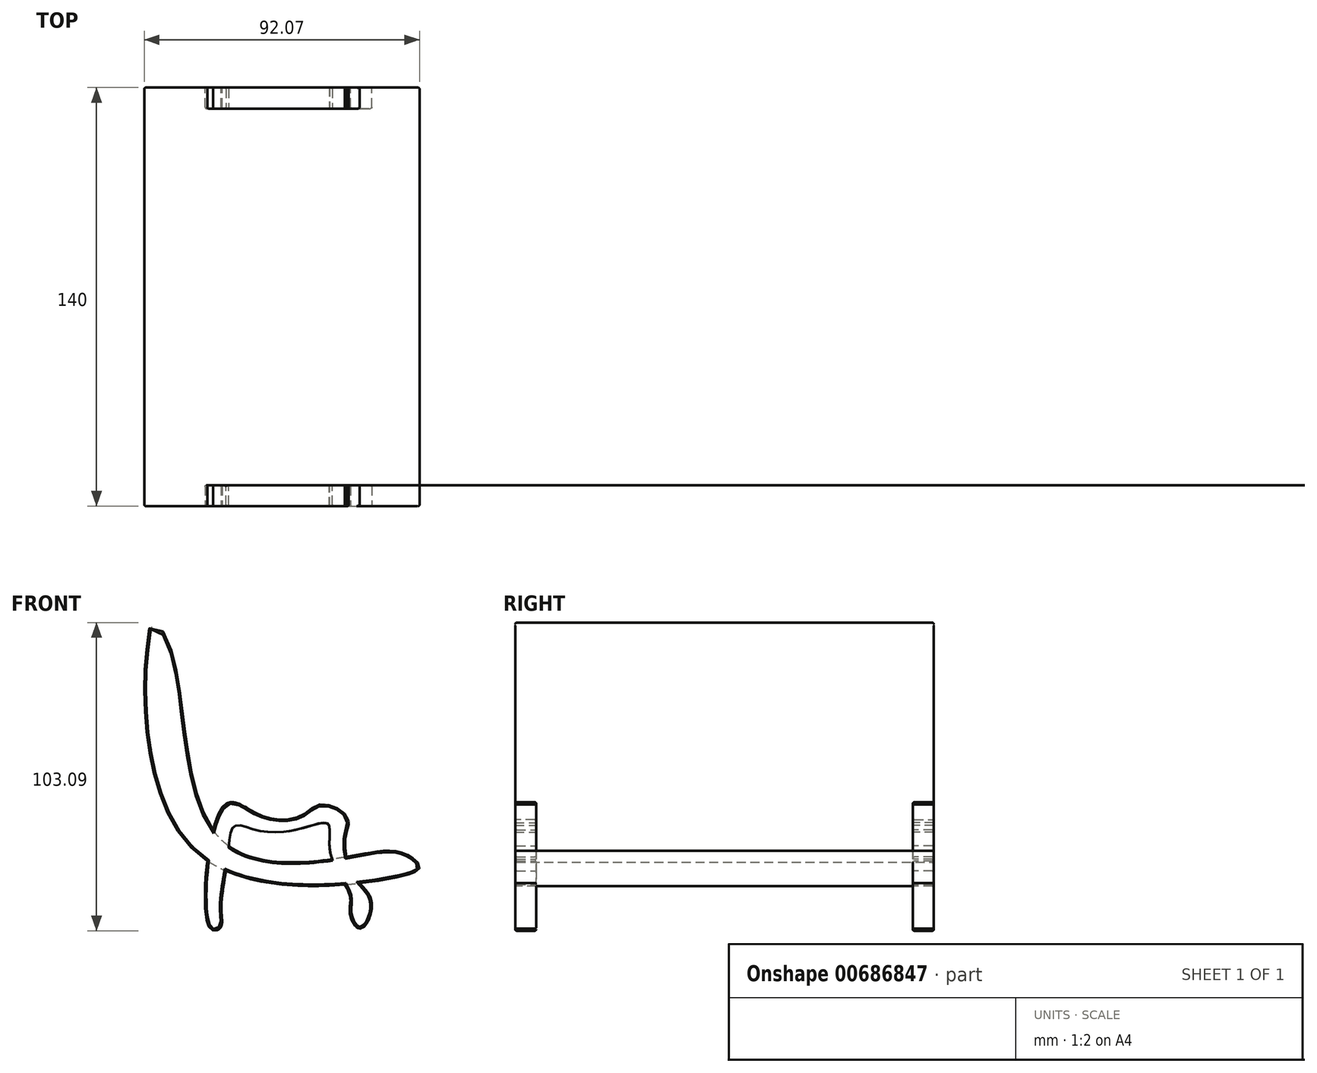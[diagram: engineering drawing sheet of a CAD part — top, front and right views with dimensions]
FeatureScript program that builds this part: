
annotation { "Feature Type Name" : "Feature", "Feature Type Description" : "" }
export const myFeature = defineFeature(function(context is Context, id is Id, definition is map)
    precondition{}
    {
        {
            var Q0;
            Q0=qCreatedBy(makeId("Front.planeOp"),FACE);
            var sketch = newSketch(context, id + "F0", { "sketchPlane" : qUnion([Q0])});
            skFitSpline(sketch, "E0", {"points": [v(-47.91, 42.75) * mm, v(-30.7, -20.37) * mm, v(37, -28.4) * mm, v(43.9, -24.96) * mm, v(38.16, -20.37) * mm, v(20.94, -21.52) * mm, v(-22.66, -15.78) * mm, v(-38.73, 46.2) * mm, v(-45.62, 56.52) * mm, v(-46.76, 51.93) * mm, v(-47.91, 42.75) * mm]});
            skSolve(sketch);
        }
        {
            var Q0;
            Q0 = qSketchRegion(id + "F0", true);
            extrude(context, id + "F1", {"entities" : qUnion([Q0]), "depth" : 70 * mm, "offsetDistance" : 25.4 * mm});
        }
        {
            var Q0;
            Q0=qCreatedBy(makeId("Front.planeOp"),FACE);
            cPlane(context, id + "F2", {"entities" : qUnion([Q0]), "cplaneType" : CPlaneType.OFFSET, "offset" : 63 * mm, "width" : 150 * mm, "height" : 150 * mm});
        }
        {
            var Q0;
            Q0=qCreatedBy(id+"F2.planeOp",FACE);
            var sketch = newSketch(context, id + "F3", { "sketchPlane" : qUnion([Q0])});
            skFitSpline(sketch, "E1", {"points": [v(-27.53, -41.38) * mm, v(-20.96, -4.2) * mm, v(-9.3, -7.84) * mm, v(4.56, -7.84) * mm, v(11.12, -4.2) * mm, v(19.87, -8.57) * mm, v(19.14, -15.13) * mm, v(22.06, -28.26) * mm, v(27.9, -37) * mm, v(24.24, -45.76) * mm, v(20.6, -40.65) * mm, v(20.6, -34.82) * mm, v(14.04, -20.23) * mm, v(13.3, -10.76) * mm, v(4.56, -12.21) * mm, v(-10.03, -12.94) * mm, v(-18.05, -11.48) * mm, v(-20.23, -21.7) * mm, v(-22.42, -39.2) * mm, v(-22.42, -45.03) * mm, v(-24.6, -46.48) * mm, v(-27.53, -41.38) * mm]});
            skSolve(sketch);
        }
        {
            var Q0;
            Q0 = qSketchRegion(id + "F3", true);
            extrude(context, id + "F4", {"entities" : qUnion([Q0]), "operationType" : NewBodyOperationType.ADD, "depth" : 7 * mm, "offsetDistance" : 25 * mm});
        }
        {
            var Q0;
            Q0=makeQuery(id+"F4.boolean.opBoolean","SPLIT",EDGE,{"disambiguationData":[OD(1.0)],"derivedFrom":makeQuery(id+"F4.opExtrude","CAP_EDGE",EDGE,{"disambiguationData":[OSD([sQuery(id+"F3.wireOp",EDGE,"E1")])],"isStart":false})});
            var Q1;
            Q1=makeQuery(id+"F4.boolean.opBoolean","SPLIT",EDGE,{"disambiguationData":[OD(0.0)],"derivedFrom":makeQuery(id+"F1.opExtrude","CAP_EDGE",EDGE,{"disambiguationData":[OSD([sQuery(id+"F0.wireOp",EDGE,"E0")])],"isStart":false})});
            var Q2;
            Q2=makeQuery(id+"F4.boolean.opBoolean","SPLIT",EDGE,{"disambiguationData":[OD(2.0)],"derivedFrom":makeQuery(id+"F1.opExtrude","CAP_EDGE",EDGE,{"disambiguationData":[OSD([sQuery(id+"F0.wireOp",EDGE,"E0")])],"isStart":false})});
            var Q3;
            Q3=makeQuery(id+"F4.boolean.opBoolean","SPLIT",EDGE,{"disambiguationData":[OD(1.0)],"derivedFrom":makeQuery(id+"F1.opExtrude","CAP_EDGE",EDGE,{"disambiguationData":[OSD([sQuery(id+"F0.wireOp",EDGE,"E0")])],"isStart":false})});
            var Q4;
            Q4=makeQuery(id+"F4.boolean.opBoolean","SPLIT",EDGE,{"disambiguationData":[OD(0.0)],"derivedFrom":makeQuery(id+"F4.opExtrude","CAP_EDGE",EDGE,{"disambiguationData":[OSD([sQuery(id+"F3.wireOp",EDGE,"E1")])],"isStart":false})});
            var Q5;
            Q5=makeQuery(id+"F4.boolean.opBoolean","SPLIT",EDGE,{"disambiguationData":[OD(3.0)],"derivedFrom":makeQuery(id+"F4.opExtrude","CAP_EDGE",EDGE,{"disambiguationData":[OSD([sQuery(id+"F3.wireOp",EDGE,"E1")])],"isStart":false})});
            var Q6;
            Q6=makeQuery(id+"F4.boolean.opBoolean","SPLIT",EDGE,{"disambiguationData":[OD(0.0)],"derivedFrom":makeQuery(id+"F4.opExtrude","CAP_EDGE",EDGE,{"disambiguationData":[OSD([sQuery(id+"F3.wireOp",EDGE,"E1")])],"isStart":true})});
            var Q7;
            Q7=makeQuery(id+"F4.boolean.opBoolean","SPLIT",EDGE,{"disambiguationData":[OD(3.0)],"derivedFrom":makeQuery(id+"F4.opExtrude","CAP_EDGE",EDGE,{"disambiguationData":[OSD([sQuery(id+"F3.wireOp",EDGE,"E1")])],"isStart":true})});
            var Q8;
            Q8=makeQuery(id+"F4.boolean.opBoolean","SPLIT",EDGE,{"disambiguationData":[OD(2.0)],"derivedFrom":makeQuery(id+"F4.opExtrude","CAP_EDGE",EDGE,{"disambiguationData":[OSD([sQuery(id+"F3.wireOp",EDGE,"E1")])],"isStart":true})});
            var Q9;
            Q9=makeQuery(id+"F4.boolean.opBoolean","SPLIT",EDGE,{"disambiguationData":[OD(3.0)],"derivedFrom":makeQuery(id+"F1.opExtrude","CAP_EDGE",EDGE,{"disambiguationData":[OSD([sQuery(id+"F0.wireOp",EDGE,"E0")])],"isStart":false})});
            fillet(context, id + "F5", {"entities" : qUnion([Q0, Q1, Q2, Q3, Q4, Q5, Q6, Q7, Q8, Q9]), "radius" : 0.5 * mm, "tangentPropagation" : true, "allowEdgeOverflow" : false});
        }
        {
            var Q0;
            Q0=makeQuery(id+"F1.opExtrude","SWEPT_BODY",BODY,{"disambiguationData":[OSD([sQuery(id+"F0.wireOp",EDGE,"E0")])]});
            var Q1;
            Q1=qCreatedBy(makeId("Front.planeOp"),FACE);
            mirror(context, id + "F6", {"operationType" : NewBodyOperationType.ADD, "entities" : qUnion([Q0]), "mirrorPlane" : qUnion([Q1])});
        }
    });
